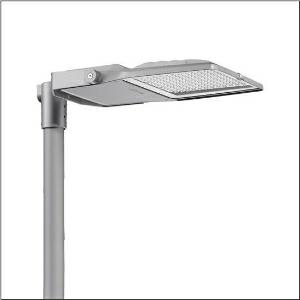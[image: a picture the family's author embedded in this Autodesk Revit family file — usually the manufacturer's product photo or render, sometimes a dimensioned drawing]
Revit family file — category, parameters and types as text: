
# Revit family: floodlight_fl_21_midi___pl52_5xa7782f4d3a_178b
name_source: partatom
category: Lighting Fixtures
units: mm (PartAtom-declared; Revit-internal decimal feet)

## family parameters
Cut with Voids When Loaded = No
Host = Face
Light Source = No
Part Type = Normal
Room Calculation Point = No
Round Connector Dimension = Use Diameter
Shared = No

## types (1)
- --- (1 x LED, 37330 lm, 270.2 W, 4000K)
    Apparent Load = 270 VA
    CIE Flux Codes = 26 60 98 100 100
    Color Rendering = 70
    Color Temperature = 4000K
    Default Elevation = 1800 mm
    Description = Floodlight FL 21 midi, floodlight, primary light control with lens, of PMMA, primary optical cover: protective disc, of toughened safety glass, transparent, light distribution: PL52, light emission: direct distribution, installation type: surface-mounted, LED, High Power LED, rated luminous flux: 37.330lm, luminous efficacy: 138lm/W, light colour: 740, colour temperature: 4000K, control gear: ECG iQ, control: optimised constant luminous flux control (CLO 2.0), Desk-Remote (wireless, voltage-free reading and setting of iQ features in the workshop via application-optimized NFC function/RFID function), Smart-Wire, Night-Set, Temp-Guard, Auto-Match, Street-Remote, with terminal, 6-pole, mains connection: 220..240V, AC, 50/60Hz, start of lifetime: 270W, end of lifetime: 286W, reduction: 138W, luminaire housing, of diecast aluminium, powder-coated, Siteco® metallic grey (DB 702S), corrosivity category C5 according to DIN EN ISO 12944, mast bracket, of steel, galvanised, powder-coated, Siteco® metallic grey (DB 702S), protection rating (complete): IP66, insulation class (complete): insulation class II (safety insulation), certification: CE, protection symbol: D, impact resistance: IK08, permissible operating ambient temperature: -40..+40°C, permissible operating ambient temperature for outdoor applications: -40..+50°C, standard: DIN EN 12944, packaging unit: 1 piece

Light Distribution: PL52
    Height = 76 mm
    Lamp = 1 x LED
    Lamp Light Flux = 37330 lm
    Lamp Power = 270.2 W
    Lamp count = 1
    Length = 657 mm
    Luminous efficacy = 138 lm/W
    Manufacturer = Siteco
    ModVariant = No
    Model = 5XA7782F4D3A
    Number of Poles = 1
    OnlyDefault = Yes
    Power Factor = 1
    Product Name = Floodlight FL 21 midi | PL52
    Product group = floodlight | pylon top
    ProductGroupID = 6101
    Protection Class = Protection class II
    Protection Degree = IP 66
    RLX_Detail_Level = 1
    RlxData = <blob elided: 153793 chars, md5=df86c561>
    Socket = socket
    Standby Power = 0 W
    System Light Flux = 37330 lm
    System Power = 270 W
    Type Comments = factory setting: luminous flux: 100 % | dim-lin: 254 | 620 mA
    Type Image = l_1007123.jpg
    URL = http://relux.com
    VarID = @adj_014127
    Voltage = 0 V
    Weight = 0.00 kg
    Width = 442 mm

## geometry (parser evidence)
native form markers: Blend x4, Sweep x15
no freeform markers — native parametric forms only
